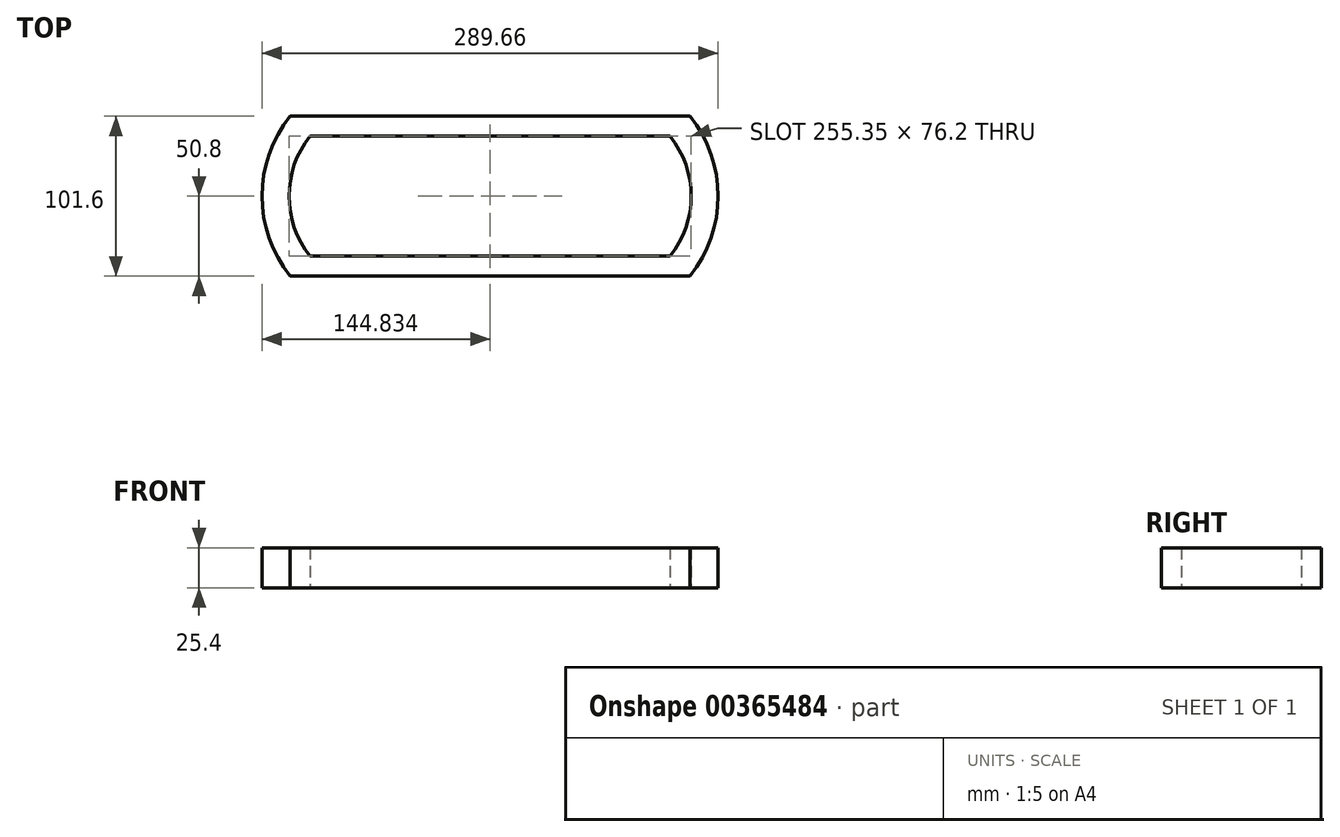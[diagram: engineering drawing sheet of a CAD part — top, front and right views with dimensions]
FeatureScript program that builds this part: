
annotation { "Feature Type Name" : "Feature", "Feature Type Description" : "" }
export const myFeature = defineFeature(function(context is Context, id is Id, definition is map)
    precondition{}
    {
        {
            var Q0;
            Q0=qCreatedBy(makeId("Top.planeOp"),FACE);
            var sketch = newSketch(context, id + "F0", { "sketchPlane" : qUnion([Q0])});
            skLineSegment(sketch, "E0.bottom", {"start": v(-95.39, 51.08) * mm, "end": v(158.61, 51.08) * mm});
            skLineSegment(sketch, "E0.top", {"start": v(-95.39, -50.52) * mm, "end": v(158.61, -50.52) * mm});
            skLineSegment(sketch, "E1.bottom", {"start": v(-82.69, 38.38) * mm, "end": v(145.91, 38.38) * mm});
            skLineSegment(sketch, "E1.top", {"start": v(-82.69, -37.82) * mm, "end": v(145.91, -37.82) * mm});
            skArc(sketch, "E2", {"start": v(158.61, -50.52) * mm, "mid": v(176.44, 0.28) * mm, "end": v(158.61, 51.08) * mm});
            skArc(sketch, "E3", {"start": v(145.91, -37.82) * mm, "mid": v(159.29, 0.28) * mm, "end": v(145.91, 38.38) * mm});
            skLineSegment(sketch, "E4", {"start": v(31.61, 38.38) * mm, "end": v(31.61, -109.37) * mm});
            skArc(sketch, "E5.MirrorCS", {"start": v(-95.39, -50.52) * mm, "mid": v(-113.22, 0.28) * mm, "end": v(-95.39, 51.08) * mm});
            skArc(sketch, "E6.MirrorCS", {"start": v(-82.69, -37.82) * mm, "mid": v(-96.06, 0.28) * mm, "end": v(-82.69, 38.38) * mm});
            skSolve(sketch);
        }
        {
            var Q0;
            Q0=makeQuery(id+"F0.imprint","IMPRINT",FACE,{"disambiguationData":[TD([[makeQuery(id+"F0.imprint","IMPRINT",EDGE,{"derivedFrom":sQuery(id+"F0.wireOp",EDGE,"E0.bottom")}),-1.0]])]});
            extrude(context, id + "F1", {"entities" : qUnion([Q0]), "depth" : 25.4 * mm});
        }
    });
